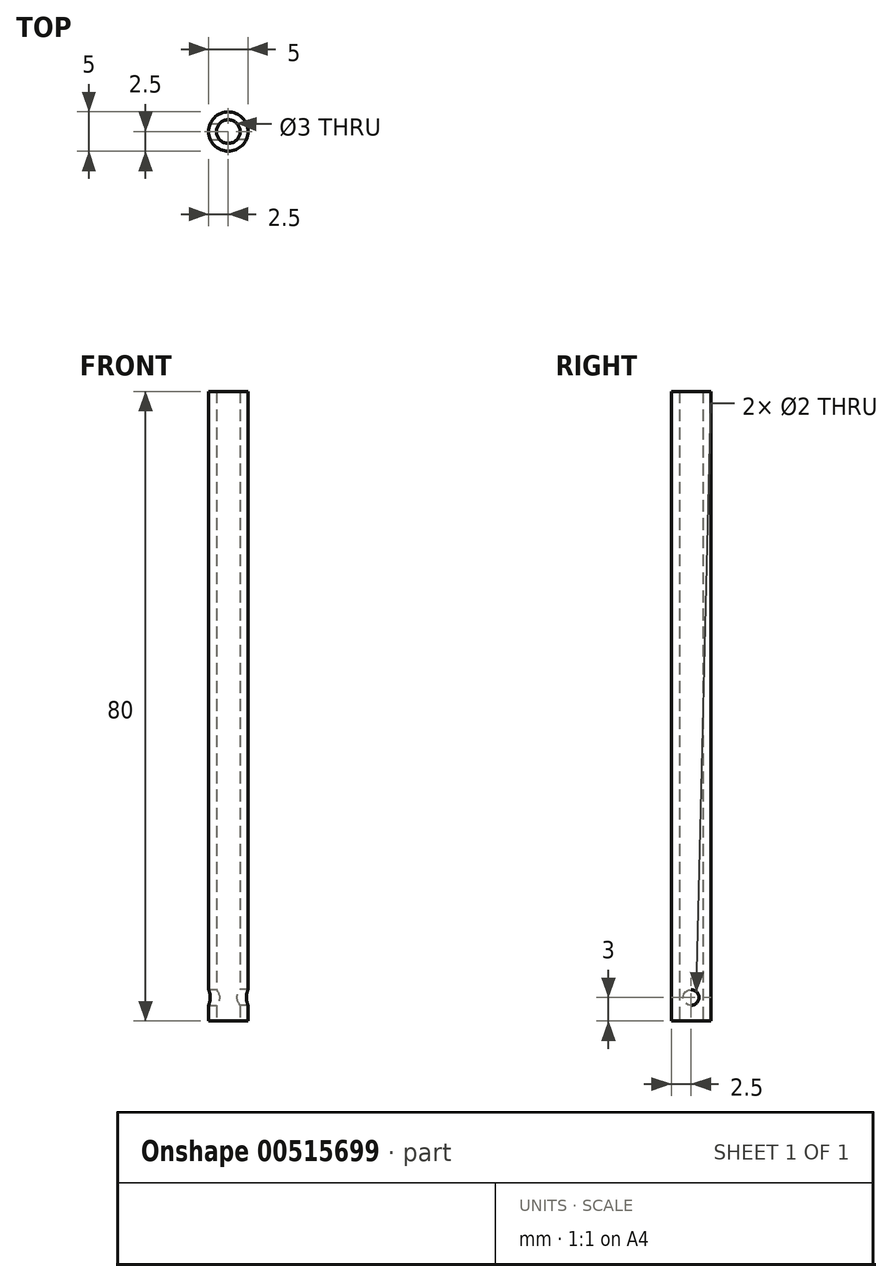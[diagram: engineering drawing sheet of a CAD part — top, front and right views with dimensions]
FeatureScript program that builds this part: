
annotation { "Feature Type Name" : "Feature", "Feature Type Description" : "" }
export const myFeature = defineFeature(function(context is Context, id is Id, definition is map)
    precondition{}
    {
        {
            var Q0;
            Q0=qCreatedBy(makeId("Top.planeOp"),FACE);
            var sketch = newSketch(context, id + "F0", { "sketchPlane" : qUnion([Q0])});
            skCircle(sketch, "E0", {"center": v(0, 0) * mm, "radius": 1.5 * mm});
            skCircle(sketch, "E1", {"center": v(0, 0) * mm, "radius": 2.5 * mm});
            skSolve(sketch);
        }
        {
            var Q0;
            Q0=makeQuery(id+"F0.imprint","IMPRINT",FACE,{"disambiguationData":[TD([[makeQuery(id+"F0.imprint","IMPRINT",EDGE,{"derivedFrom":sQuery(id+"F0.wireOp",EDGE,"E0")}),-1.0]])]});
            extrude(context, id + "F1", {"entities" : qUnion([Q0]), "depth" : 80 * mm, "offsetDistance" : 25 * mm});
        }
        {
            var Q0;
            Q0=qCreatedBy(makeId("Right.planeOp"),FACE);
            var sketch = newSketch(context, id + "F2", { "sketchPlane" : qUnion([Q0])});
            skLineSegment(sketch, "E2", {"start": v(0, 0) * mm, "end": v(0, 3) * mm});
            skCircle(sketch, "E3", {"center": v(0, 3) * mm, "radius": 1 * mm});
            skSolve(sketch);
        }
        {
            var Q0;
            Q0=sQuery(id+"F2.wireOp",VERTEX,"E2.end");
            var Q1;
            Q1=makeQuery(id+"F1.opExtrude","SWEPT_BODY",BODY,{"disambiguationData":[OSD([sQuery(id+"F0.wireOp",EDGE,"E0"),sQuery(id+"F0.wireOp",EDGE,"E1")])]});
            hole(context, id + "F3", {"style" : HoleStyle.SIMPLE, "endStyle" : HoleEndStyle.THROUGH, "holeDiameter" : 2 * mm, "isTappedThrough" : true, "tappedDepth" : 12 * mm, "tapClearance" : 3, "locations" : qUnion([Q0]), "scope" : qUnion([Q1])});
        }
        {
            var Q0;
            Q0=sQuery(id+"F2.wireOp",VERTEX,"E3.center");
            var Q1;
            Q1=makeQuery(id+"F1.opExtrude","SWEPT_BODY",BODY,{"disambiguationData":[OSD([sQuery(id+"F0.wireOp",EDGE,"E0"),sQuery(id+"F0.wireOp",EDGE,"E1")])]});
            hole(context, id + "F4", {"style" : HoleStyle.SIMPLE, "endStyle" : HoleEndStyle.THROUGH, "oppositeDirection" : true, "holeDiameter" : 2 * mm, "isTappedThrough" : true, "tappedDepth" : 12 * mm, "tapClearance" : 3, "locations" : qUnion([Q0]), "scope" : qUnion([Q1])});
        }
    });
